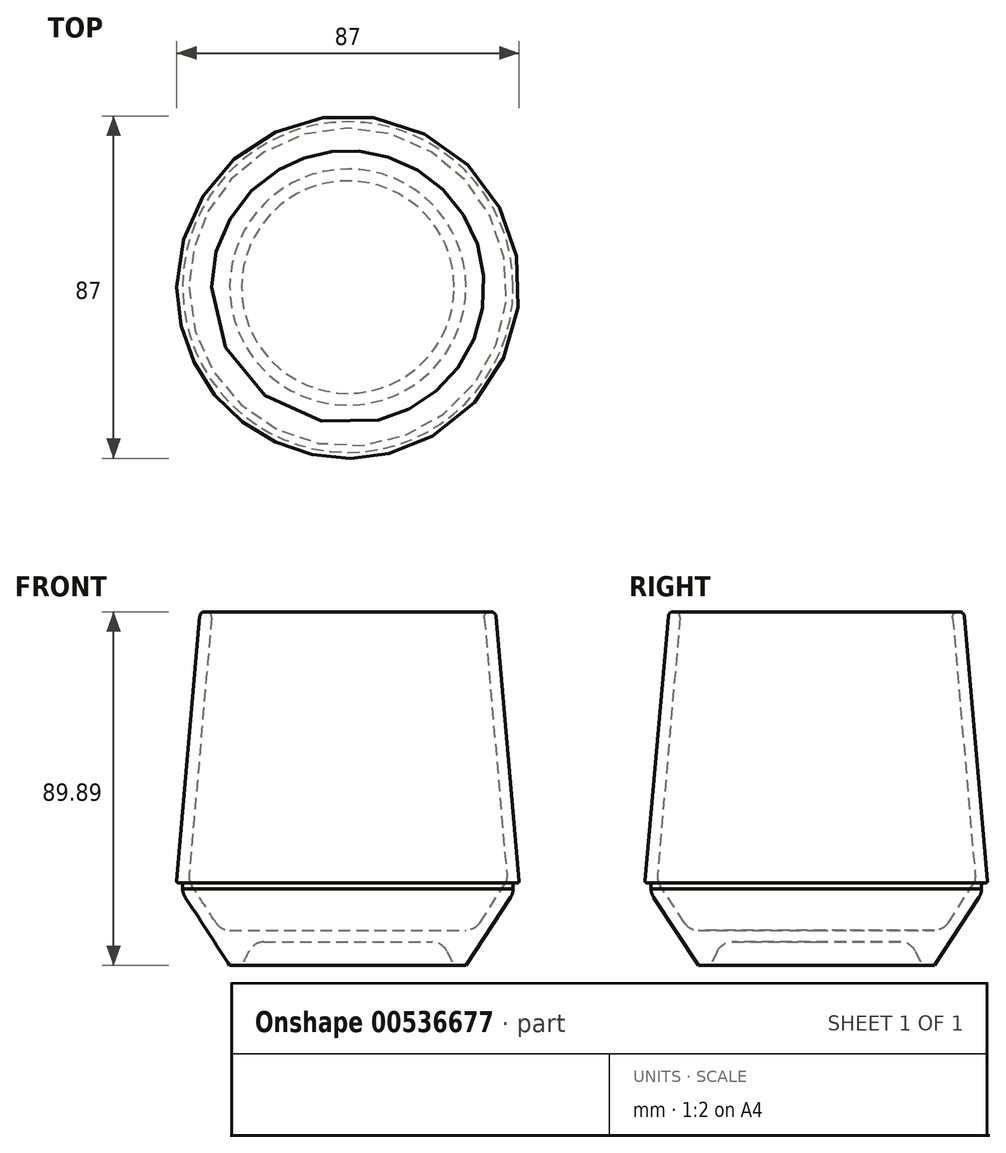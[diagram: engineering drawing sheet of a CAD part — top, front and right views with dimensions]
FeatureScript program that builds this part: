
annotation { "Feature Type Name" : "Feature", "Feature Type Description" : "" }
export const myFeature = defineFeature(function(context is Context, id is Id, definition is map)
    precondition{}
    {
        {
            var Q0;
            Q0=qCreatedBy(makeId("Front.planeOp"),FACE);
            var sketch = newSketch(context, id + "F0", { "sketchPlane" : qUnion([Q0])});
            skLineSegment(sketch, "E0", {"start": v(0, 6) * mm, "end": v(21.4, 6) * mm});
            skLineSegment(sketch, "E1", {"start": v(25.17, 3.67) * mm, "end": v(27, 0) * mm});
            skLineSegment(sketch, "E2", {"start": v(27, 0) * mm, "end": v(30, 0) * mm});
            skLineSegment(sketch, "E3", {"start": v(30, 0) * mm, "end": v(41.32, 17.37) * mm});
            skLineSegment(sketch, "E4", {"start": v(43.5, 21.54) * mm, "end": v(37.62, 88.7) * mm});
            skLineSegment(sketch, "E5", {"start": v(36.22, 89.89) * mm, "end": v(35.82, 89.85) * mm});
            skLineSegment(sketch, "E6", {"start": v(34.64, 88.44) * mm, "end": v(40.36, 23.03) * mm});
            skLineSegment(sketch, "E7", {"start": v(39.7, 20.36) * mm, "end": v(33.53, 10.91) * mm});
            skLineSegment(sketch, "E8", {"start": v(30, 9) * mm, "end": v(0, 9) * mm});
            skLineSegment(sketch, "E9", {"start": v(0, 9) * mm, "end": v(0, 6) * mm});
            skPoint(sketch, "E10.visualSharp", {"position": v(24, 6) * mm});
            skArc(sketch, "E10.filletArc", {"start": v(25.17, 3.67) * mm, "mid": v(23.61, 5.37) * mm, "end": v(21.4, 6) * mm});
            skPoint(sketch, "E11.visualSharp", {"position": v(32.29, 9) * mm});
            skArc(sketch, "E11.filletArc", {"start": v(30, 9) * mm, "mid": v(32, 9.5) * mm, "end": v(33.53, 10.91) * mm});
            skPoint(sketch, "E12.visualSharp", {"position": v(40.49, 21.58) * mm});
            skArc(sketch, "E12.filletArc", {"start": v(39.7, 20.36) * mm, "mid": v(40.25, 21.64) * mm, "end": v(40.36, 23.03) * mm});
            skPoint(sketch, "E13.visualSharp", {"position": v(41.56, 17.74) * mm});
            skArc(sketch, "E13.filletArc", {"start": v(41.32, 17.37) * mm, "mid": v(41.8, 18.39) * mm, "end": v(42, 19.5) * mm});
            skPoint(sketch, "E14.visualSharp", {"position": v(37.51, 90) * mm});
            skArc(sketch, "E14.filletArc", {"start": v(37.62, 88.7) * mm, "mid": v(37.16, 89.59) * mm, "end": v(36.22, 89.89) * mm});
            skPoint(sketch, "E15.visualSharp", {"position": v(34.52, 89.74) * mm});
            skArc(sketch, "E15.filletArc", {"start": v(35.82, 89.85) * mm, "mid": v(34.93, 89.4) * mm, "end": v(34.64, 88.44) * mm});
            skLineSegment(sketch, "E16", {"start": v(43.5, 21.54) * mm, "end": v(43.5, 90) * mm, "construction": true});
            skLineSegment(sketch, "E17", {"start": v(0, 0) * mm, "end": v(0, 88.7) * mm, "construction": true});
            skLineSegment(sketch, "E18", {"start": v(42, 19.5) * mm, "end": v(42, 20.5) * mm});
            skArc(sketch, "E19", {"start": v(43, 21) * mm, "mid": v(43.37, 21.16) * mm, "end": v(43.5, 21.54) * mm});
            skLineSegment(sketch, "E20", {"start": v(43, 21) * mm, "end": v(42.5, 21) * mm});
            skArc(sketch, "E21", {"start": v(42.5, 21) * mm, "mid": v(42.15, 20.85) * mm, "end": v(42, 20.5) * mm});
            skSolve(sketch);
        }
        {
            var Q0;
            Q0=qSketchRegion(id+"F0",true);
            var Q1;
            Q1=sQuery(id+"F0.wireOp",EDGE,"E17");
            revolve(context, id + "F1", {"entities" : qUnion([Q0]), "axis" : qUnion([Q1]), "revolveType" : RevolveType.FULL});
        }
    });
